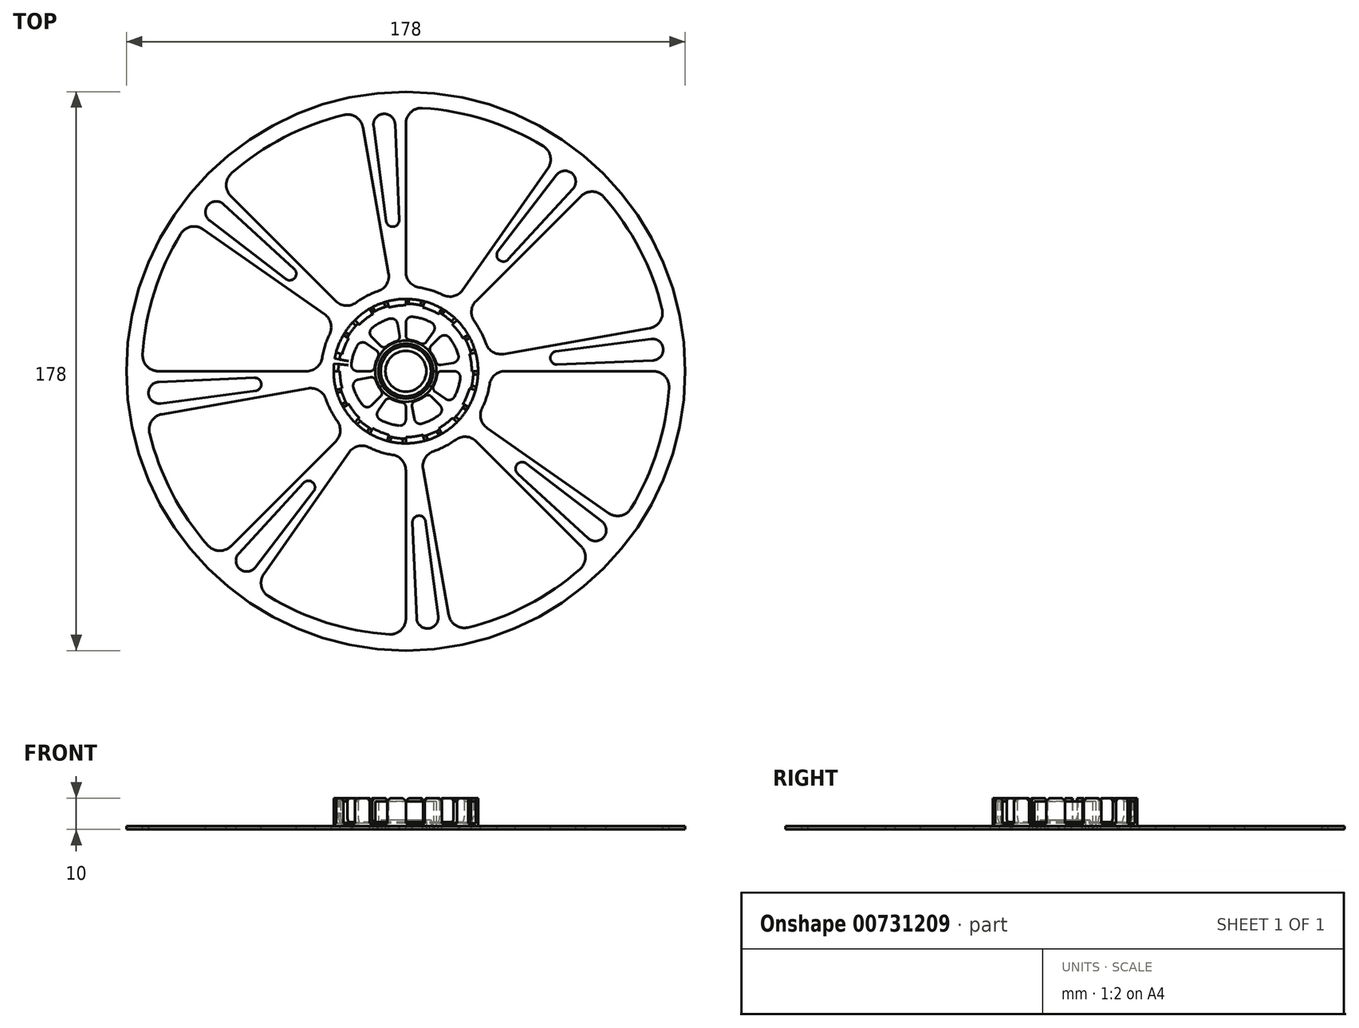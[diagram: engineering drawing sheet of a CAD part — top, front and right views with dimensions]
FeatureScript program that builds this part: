
annotation { "Feature Type Name" : "Feature", "Feature Type Description" : "" }
export const myFeature = defineFeature(function(context is Context, id is Id, definition is map)
    precondition{}
    {
        {
            var Q0;
            Q0=qCreatedBy(makeId("Top.planeOp"),FACE);
            var sketch = newSketch(context, id + "F0", { "sketchPlane" : qUnion([Q0])});
            skCircle(sketch, "E0", {"center": v(0, 0) * mm, "radius": 89 * mm});
            skCircle(sketch, "E1", {"center": v(0, 0) * mm, "radius": 6.5 * mm});
            skSolve(sketch);
        }
        {
            var Q0;
            Q0=qSketchRegion(id+"F0",true);
            extrude(context, id + "F1", {"entities" : qUnion([Q0]), "depth" : 1 * mm, "offsetDistance" : 25 * mm});
        }
        {
            var Q0;
            Q0=makeQuery(id+"F1.opExtrude","CAP_FACE",FACE,{"disambiguationData":[OSD([sQuery(id+"F0.wireOp",EDGE,"E0"),sQuery(id+"F0.wireOp",EDGE,"E1")])],"isStart":false});
            var sketch = newSketch(context, id + "F2", { "sketchPlane" : qUnion([Q0])});
            skCircle(sketch, "E2", {"center": v(0, 0) * mm, "radius": 23 * mm});
            skCircle(sketch, "E3.0", {"center": v(0, 0) * mm, "radius": 21.5 * mm});
            skSolve(sketch);
        }
        {
            var Q0;
            Q0=qSketchRegion(id+"F2",true);
            extrude(context, id + "F3", {"entities" : qUnion([Q0]), "operationType" : NewBodyOperationType.ADD, "depth" : 9 * mm, "offsetDistance" : 25 * mm});
        }
        {
            var Q0;
            Q0=makeQuery(id+"F3.opExtrude","CAP_EDGE",EDGE,{"disambiguationData":[OSD([sQuery(id+"F2.wireOp",EDGE,"E3.0")])],"isStart":true});
            fillet(context, id + "F4", {"entities" : qUnion([Q0]), "radius" : 3 * mm, "tangentPropagation" : true, "allowEdgeOverflow" : false});
        }
        {
            var Q0;
            {var subQ0=sQuery(id+"F0.wireOp",EDGE,"E0");Q0=makeQuery(id+"F3.boolean.opBoolean","SPLIT",FACE,{"disambiguationData":[TD([makeQuery(id+"F1.opExtrude","SWEPT_FACE",FACE,{"disambiguationData":[OSD([subQ0])]})])],"derivedFrom":makeQuery(id+"F1.opExtrude","CAP_FACE",FACE,{"disambiguationData":[OSD([subQ0,sQuery(id+"F0.wireOp",EDGE,"E1")])],"isStart":false})});}
            var sketch = newSketch(context, id + "F5", { "sketchPlane" : qUnion([Q0])});
            skLineSegment(sketch, "E4", {"start": v(-78.84, 0) * mm, "end": v(-31.6, 0) * mm});
            skLineSegment(sketch, "E5", {"start": v(-64.58, 45.22) * mm, "end": v(-25.9, 18.13) * mm});
            skPoint(sketch, "E6.center", {"position": v(0, 0) * mm});
            skArc(sketch, "E7", {"start": v(-26.67, 4.22) * mm, "mid": v(-25.75, 8.12) * mm, "end": v(-24.27, 11.84) * mm});
            skArc(sketch, "E8", {"start": v(-83.83, 5.32) * mm, "mid": v(-80.11, 25.26) * mm, "end": v(-71.72, 43.73) * mm});
            skPoint(sketch, "E9.visualSharp", {"position": v(-68.8, 48.18) * mm});
            skArc(sketch, "E9.filletArc", {"start": v(-64.58, 45.22) * mm, "mid": v(-68.47, 46.02) * mm, "end": v(-71.72, 43.73) * mm});
            skPoint(sketch, "E10.visualSharp", {"position": v(-84, 0) * mm});
            skArc(sketch, "E10.filletArc", {"start": v(-83.83, 5.32) * mm, "mid": v(-82.49, 1.58) * mm, "end": v(-78.84, 0) * mm});
            skPoint(sketch, "E11.visualSharp", {"position": v(-22.12, 15.49) * mm});
            skArc(sketch, "E11.filletArc", {"start": v(-24.27, 11.84) * mm, "mid": v(-23.92, 15.28) * mm, "end": v(-25.9, 18.13) * mm});
            skPoint(sketch, "E12.visualSharp", {"position": v(-27, 0) * mm});
            skArc(sketch, "E12.filletArc", {"start": v(-31.6, 0) * mm, "mid": v(-28.36, 1.2) * mm, "end": v(-26.67, 4.22) * mm});
            skArc(sketch, "E13.1.0", {"start": v(-63.04, -55.52) * mm, "mid": v(-74.5, -38.79) * mm, "end": v(-81.63, -19.8) * mm});
            skArc(sketch, "E13.1.1", {"start": v(-21.84, -15.87) * mm, "mid": v(-23.95, -12.47) * mm, "end": v(-25.53, -8.79) * mm});
            skPoint(sketch, "E13.1.2", {"position": v(-26.59, -4.69) * mm});
            skPoint(sketch, "E13.1.3", {"position": v(-59.4, -59.4) * mm});
            skPoint(sketch, "E13.1.4", {"position": v(-19.1, -19.1) * mm});
            skLineSegment(sketch, "E13.1.5", {"start": v(-31.13, -5.49) * mm, "end": v(-77.64, -13.7) * mm});
            skPoint(sketch, "E13.1.6", {"position": v(-82.72, -14.59) * mm});
            skLineSegment(sketch, "E13.1.7", {"start": v(-55.75, -55.75) * mm, "end": v(-22.35, -22.35) * mm});
            skArc(sketch, "E13.1.8", {"start": v(-63.04, -55.52) * mm, "mid": v(-59.44, -57.21) * mm, "end": v(-55.75, -55.75) * mm});
            skArc(sketch, "E13.1.9", {"start": v(-22.35, -22.35) * mm, "mid": v(-20.9, -19.2) * mm, "end": v(-21.84, -15.87) * mm});
            skArc(sketch, "E13.1.10", {"start": v(-25.53, -8.79) * mm, "mid": v(-27.72, -6.1) * mm, "end": v(-31.13, -5.49) * mm});
            skArc(sketch, "E13.1.11", {"start": v(-77.64, -13.7) * mm, "mid": v(-80.96, -15.88) * mm, "end": v(-81.63, -19.8) * mm});
            skArc(sketch, "E13.2.0", {"start": v(-5.32, -83.83) * mm, "mid": v(-25.26, -80.11) * mm, "end": v(-43.73, -71.72) * mm});
            skArc(sketch, "E13.2.1", {"start": v(-4.22, -26.67) * mm, "mid": v(-8.12, -25.75) * mm, "end": v(-11.84, -24.27) * mm});
            skPoint(sketch, "E13.2.2", {"position": v(-15.49, -22.12) * mm});
            skPoint(sketch, "E13.2.3", {"position": v(0, -84) * mm});
            skPoint(sketch, "E13.2.4", {"position": v(0, -27) * mm});
            skLineSegment(sketch, "E13.2.5", {"start": v(-45.22, -64.58) * mm, "end": v(-18.13, -25.9) * mm});
            skPoint(sketch, "E13.2.6", {"position": v(-48.18, -68.8) * mm});
            skLineSegment(sketch, "E13.2.7", {"start": v(0, -78.84) * mm, "end": v(0, -31.6) * mm});
            skArc(sketch, "E13.2.8", {"start": v(-5.32, -83.83) * mm, "mid": v(-1.58, -82.49) * mm, "end": v(0, -78.84) * mm});
            skArc(sketch, "E13.2.9", {"start": v(0, -31.6) * mm, "mid": v(-1.2, -28.36) * mm, "end": v(-4.22, -26.67) * mm});
            skArc(sketch, "E13.2.10", {"start": v(-11.84, -24.27) * mm, "mid": v(-15.28, -23.92) * mm, "end": v(-18.13, -25.9) * mm});
            skArc(sketch, "E13.2.11", {"start": v(-45.22, -64.58) * mm, "mid": v(-46.02, -68.47) * mm, "end": v(-43.73, -71.72) * mm});
            skArc(sketch, "E13.3.0", {"start": v(55.52, -63.04) * mm, "mid": v(38.79, -74.5) * mm, "end": v(19.8, -81.63) * mm});
            skArc(sketch, "E13.3.1", {"start": v(15.87, -21.84) * mm, "mid": v(12.47, -23.95) * mm, "end": v(8.79, -25.53) * mm});
            skPoint(sketch, "E13.3.2", {"position": v(4.69, -26.59) * mm});
            skPoint(sketch, "E13.3.3", {"position": v(59.4, -59.4) * mm});
            skPoint(sketch, "E13.3.4", {"position": v(19.1, -19.1) * mm});
            skLineSegment(sketch, "E13.3.5", {"start": v(5.49, -31.13) * mm, "end": v(13.7, -77.64) * mm});
            skPoint(sketch, "E13.3.6", {"position": v(14.59, -82.72) * mm});
            skLineSegment(sketch, "E13.3.7", {"start": v(55.75, -55.75) * mm, "end": v(22.35, -22.35) * mm});
            skArc(sketch, "E13.3.8", {"start": v(55.52, -63.04) * mm, "mid": v(57.21, -59.44) * mm, "end": v(55.75, -55.75) * mm});
            skArc(sketch, "E13.3.9", {"start": v(22.35, -22.35) * mm, "mid": v(19.2, -20.9) * mm, "end": v(15.87, -21.84) * mm});
            skArc(sketch, "E13.3.10", {"start": v(8.79, -25.53) * mm, "mid": v(6.1, -27.72) * mm, "end": v(5.49, -31.13) * mm});
            skArc(sketch, "E13.3.11", {"start": v(13.7, -77.64) * mm, "mid": v(15.88, -80.96) * mm, "end": v(19.8, -81.63) * mm});
            skArc(sketch, "E13.4.0", {"start": v(83.83, -5.32) * mm, "mid": v(80.11, -25.26) * mm, "end": v(71.72, -43.73) * mm});
            skArc(sketch, "E13.4.1", {"start": v(26.67, -4.22) * mm, "mid": v(25.75, -8.12) * mm, "end": v(24.27, -11.84) * mm});
            skPoint(sketch, "E13.4.2", {"position": v(22.12, -15.49) * mm});
            skPoint(sketch, "E13.4.3", {"position": v(84, 0) * mm});
            skPoint(sketch, "E13.4.4", {"position": v(27, 0) * mm});
            skLineSegment(sketch, "E13.4.5", {"start": v(64.58, -45.22) * mm, "end": v(25.9, -18.13) * mm});
            skPoint(sketch, "E13.4.6", {"position": v(68.8, -48.18) * mm});
            skLineSegment(sketch, "E13.4.7", {"start": v(78.84, 0) * mm, "end": v(31.6, 0) * mm});
            skArc(sketch, "E13.4.8", {"start": v(83.83, -5.32) * mm, "mid": v(82.49, -1.58) * mm, "end": v(78.84, 0) * mm});
            skArc(sketch, "E13.4.9", {"start": v(31.6, 0) * mm, "mid": v(28.36, -1.2) * mm, "end": v(26.67, -4.22) * mm});
            skArc(sketch, "E13.4.10", {"start": v(24.27, -11.84) * mm, "mid": v(23.92, -15.28) * mm, "end": v(25.9, -18.13) * mm});
            skArc(sketch, "E13.4.11", {"start": v(64.58, -45.22) * mm, "mid": v(68.47, -46.02) * mm, "end": v(71.72, -43.73) * mm});
            skArc(sketch, "E13.5.0", {"start": v(63.04, 55.52) * mm, "mid": v(74.5, 38.79) * mm, "end": v(81.63, 19.8) * mm});
            skArc(sketch, "E13.5.1", {"start": v(21.84, 15.87) * mm, "mid": v(23.95, 12.47) * mm, "end": v(25.53, 8.79) * mm});
            skPoint(sketch, "E13.5.2", {"position": v(26.59, 4.69) * mm});
            skPoint(sketch, "E13.5.3", {"position": v(59.4, 59.4) * mm});
            skPoint(sketch, "E13.5.4", {"position": v(19.1, 19.1) * mm});
            skLineSegment(sketch, "E13.5.5", {"start": v(31.13, 5.49) * mm, "end": v(77.64, 13.7) * mm});
            skPoint(sketch, "E13.5.6", {"position": v(82.72, 14.59) * mm});
            skLineSegment(sketch, "E13.5.7", {"start": v(55.75, 55.75) * mm, "end": v(22.35, 22.35) * mm});
            skArc(sketch, "E13.5.8", {"start": v(63.04, 55.52) * mm, "mid": v(59.44, 57.21) * mm, "end": v(55.75, 55.75) * mm});
            skArc(sketch, "E13.5.9", {"start": v(22.35, 22.35) * mm, "mid": v(20.9, 19.2) * mm, "end": v(21.84, 15.87) * mm});
            skArc(sketch, "E13.5.10", {"start": v(25.53, 8.79) * mm, "mid": v(27.72, 6.1) * mm, "end": v(31.13, 5.49) * mm});
            skArc(sketch, "E13.5.11", {"start": v(77.64, 13.7) * mm, "mid": v(80.96, 15.88) * mm, "end": v(81.63, 19.8) * mm});
            skArc(sketch, "E13.6.0", {"start": v(5.32, 83.83) * mm, "mid": v(25.26, 80.11) * mm, "end": v(43.73, 71.72) * mm});
            skArc(sketch, "E13.6.1", {"start": v(4.22, 26.67) * mm, "mid": v(8.12, 25.75) * mm, "end": v(11.84, 24.27) * mm});
            skPoint(sketch, "E13.6.2", {"position": v(15.49, 22.12) * mm});
            skPoint(sketch, "E13.6.3", {"position": v(0, 84) * mm});
            skPoint(sketch, "E13.6.4", {"position": v(0, 27) * mm});
            skLineSegment(sketch, "E13.6.5", {"start": v(45.22, 64.58) * mm, "end": v(18.13, 25.9) * mm});
            skPoint(sketch, "E13.6.6", {"position": v(48.18, 68.8) * mm});
            skLineSegment(sketch, "E13.6.7", {"start": v(0, 78.84) * mm, "end": v(0, 31.6) * mm});
            skArc(sketch, "E13.6.8", {"start": v(5.32, 83.83) * mm, "mid": v(1.58, 82.49) * mm, "end": v(0, 78.84) * mm});
            skArc(sketch, "E13.6.9", {"start": v(0, 31.6) * mm, "mid": v(1.2, 28.36) * mm, "end": v(4.22, 26.67) * mm});
            skArc(sketch, "E13.6.10", {"start": v(11.84, 24.27) * mm, "mid": v(15.28, 23.92) * mm, "end": v(18.13, 25.9) * mm});
            skArc(sketch, "E13.6.11", {"start": v(45.22, 64.58) * mm, "mid": v(46.02, 68.47) * mm, "end": v(43.73, 71.72) * mm});
            skArc(sketch, "E13.7.0", {"start": v(-55.52, 63.04) * mm, "mid": v(-38.79, 74.5) * mm, "end": v(-19.8, 81.63) * mm});
            skArc(sketch, "E13.7.1", {"start": v(-15.87, 21.84) * mm, "mid": v(-12.47, 23.95) * mm, "end": v(-8.79, 25.53) * mm});
            skPoint(sketch, "E13.7.2", {"position": v(-4.69, 26.59) * mm});
            skPoint(sketch, "E13.7.3", {"position": v(-59.4, 59.4) * mm});
            skPoint(sketch, "E13.7.4", {"position": v(-19.1, 19.1) * mm});
            skLineSegment(sketch, "E13.7.5", {"start": v(-5.49, 31.13) * mm, "end": v(-13.7, 77.64) * mm});
            skPoint(sketch, "E13.7.6", {"position": v(-14.59, 82.72) * mm});
            skLineSegment(sketch, "E13.7.7", {"start": v(-55.75, 55.75) * mm, "end": v(-22.35, 22.35) * mm});
            skArc(sketch, "E13.7.8", {"start": v(-55.52, 63.04) * mm, "mid": v(-57.21, 59.44) * mm, "end": v(-55.75, 55.75) * mm});
            skArc(sketch, "E13.7.9", {"start": v(-22.35, 22.35) * mm, "mid": v(-19.2, 20.9) * mm, "end": v(-15.87, 21.84) * mm});
            skArc(sketch, "E13.7.10", {"start": v(-8.79, 25.53) * mm, "mid": v(-6.1, 27.72) * mm, "end": v(-5.49, 31.13) * mm});
            skArc(sketch, "E13.7.11", {"start": v(-13.7, 77.64) * mm, "mid": v(-15.88, 80.96) * mm, "end": v(-19.8, 81.63) * mm});
            skLineSegment(sketch, "E14", {"start": v(-15.37, 0) * mm, "end": v(-11.4, 0) * mm});
            skLineSegment(sketch, "E15", {"start": v(-12.6, 8.82) * mm, "end": v(-9.34, 6.54) * mm});
            skArc(sketch, "E16", {"start": v(-9.91, 1.3) * mm, "mid": v(-9.54, 3) * mm, "end": v(-8.87, 4.62) * mm});
            skArc(sketch, "E17", {"start": v(-17.35, 2.26) * mm, "mid": v(-16.7, 5.26) * mm, "end": v(-15.51, 8.1) * mm});
            skPoint(sketch, "E18.visualSharp", {"position": v(-14.34, 10.04) * mm});
            skArc(sketch, "E18.filletArc", {"start": v(-12.6, 8.82) * mm, "mid": v(-14.21, 9.12) * mm, "end": v(-15.51, 8.1) * mm});
            skPoint(sketch, "E19.visualSharp", {"position": v(-17.5, 0) * mm});
            skArc(sketch, "E19.filletArc", {"start": v(-17.35, 2.26) * mm, "mid": v(-16.87, 0.68) * mm, "end": v(-15.37, 0) * mm});
            skPoint(sketch, "E20.visualSharp", {"position": v(-10, 0) * mm});
            skArc(sketch, "E20.filletArc", {"start": v(-11.4, 0) * mm, "mid": v(-10.41, 0.37) * mm, "end": v(-9.91, 1.3) * mm});
            skPoint(sketch, "E21.visualSharp", {"position": v(-8.2, 5.74) * mm});
            skArc(sketch, "E21.filletArc", {"start": v(-8.87, 4.62) * mm, "mid": v(-8.74, 5.67) * mm, "end": v(-9.34, 6.54) * mm});
            skPoint(sketch, "E22.1.0", {"position": v(-12.37, -12.37) * mm});
            skPoint(sketch, "E22.1.1", {"position": v(-17.23, -3.04) * mm});
            skArc(sketch, "E22.1.2", {"start": v(-13.87, -10.67) * mm, "mid": v(-15.52, -8.08) * mm, "end": v(-16.7, -5.24) * mm});
            skArc(sketch, "E22.1.3", {"start": v(-7.93, -6.09) * mm, "mid": v(-8.87, -4.62) * mm, "end": v(-9.54, -3) * mm});
            skPoint(sketch, "E22.1.4", {"position": v(-7.07, -7.07) * mm});
            skLineSegment(sketch, "E22.1.5", {"start": v(-11.23, -1.98) * mm, "end": v(-15.14, -2.67) * mm});
            skLineSegment(sketch, "E22.1.6", {"start": v(-10.87, -10.87) * mm, "end": v(-8.06, -8.06) * mm});
            skArc(sketch, "E22.1.7", {"start": v(-13.87, -10.67) * mm, "mid": v(-12.41, -11.45) * mm, "end": v(-10.87, -10.87) * mm});
            skArc(sketch, "E22.1.8", {"start": v(-15.14, -2.67) * mm, "mid": v(-16.5, -3.6) * mm, "end": v(-16.7, -5.24) * mm});
            skPoint(sketch, "E22.1.9", {"position": v(-9.85, -1.74) * mm});
            skArc(sketch, "E22.1.10", {"start": v(-8.06, -8.06) * mm, "mid": v(-7.63, -7.1) * mm, "end": v(-7.93, -6.09) * mm});
            skArc(sketch, "E22.1.11", {"start": v(-9.54, -3) * mm, "mid": v(-10.19, -2.17) * mm, "end": v(-11.23, -1.98) * mm});
            skPoint(sketch, "E22.2.0", {"position": v(0, -17.5) * mm});
            skPoint(sketch, "E22.2.1", {"position": v(-10.04, -14.34) * mm});
            skArc(sketch, "E22.2.2", {"start": v(-2.26, -17.35) * mm, "mid": v(-5.26, -16.7) * mm, "end": v(-8.1, -15.51) * mm});
            skArc(sketch, "E22.2.3", {"start": v(-1.3, -9.91) * mm, "mid": v(-3, -9.54) * mm, "end": v(-4.62, -8.87) * mm});
            skPoint(sketch, "E22.2.4", {"position": v(0, -10) * mm});
            skLineSegment(sketch, "E22.2.5", {"start": v(-8.82, -12.6) * mm, "end": v(-6.54, -9.34) * mm});
            skLineSegment(sketch, "E22.2.6", {"start": v(0, -15.37) * mm, "end": v(0, -11.4) * mm});
            skArc(sketch, "E22.2.7", {"start": v(-2.26, -17.35) * mm, "mid": v(-0.68, -16.87) * mm, "end": v(0, -15.37) * mm});
            skArc(sketch, "E22.2.8", {"start": v(-8.82, -12.6) * mm, "mid": v(-9.12, -14.21) * mm, "end": v(-8.1, -15.51) * mm});
            skPoint(sketch, "E22.2.9", {"position": v(-5.74, -8.2) * mm});
            skArc(sketch, "E22.2.10", {"start": v(0, -11.4) * mm, "mid": v(-0.37, -10.41) * mm, "end": v(-1.3, -9.91) * mm});
            skArc(sketch, "E22.2.11", {"start": v(-4.62, -8.87) * mm, "mid": v(-5.67, -8.74) * mm, "end": v(-6.54, -9.34) * mm});
            skPoint(sketch, "E22.3.0", {"position": v(12.37, -12.37) * mm});
            skPoint(sketch, "E22.3.1", {"position": v(3.04, -17.23) * mm});
            skArc(sketch, "E22.3.2", {"start": v(10.67, -13.87) * mm, "mid": v(8.08, -15.52) * mm, "end": v(5.24, -16.7) * mm});
            skArc(sketch, "E22.3.3", {"start": v(6.09, -7.93) * mm, "mid": v(4.62, -8.87) * mm, "end": v(3, -9.54) * mm});
            skPoint(sketch, "E22.3.4", {"position": v(7.07, -7.07) * mm});
            skLineSegment(sketch, "E22.3.5", {"start": v(1.98, -11.23) * mm, "end": v(2.67, -15.14) * mm});
            skLineSegment(sketch, "E22.3.6", {"start": v(10.87, -10.87) * mm, "end": v(8.06, -8.06) * mm});
            skArc(sketch, "E22.3.7", {"start": v(10.67, -13.87) * mm, "mid": v(11.45, -12.41) * mm, "end": v(10.87, -10.87) * mm});
            skArc(sketch, "E22.3.8", {"start": v(2.67, -15.14) * mm, "mid": v(3.6, -16.5) * mm, "end": v(5.24, -16.7) * mm});
            skPoint(sketch, "E22.3.9", {"position": v(1.74, -9.85) * mm});
            skArc(sketch, "E22.3.10", {"start": v(8.06, -8.06) * mm, "mid": v(7.1, -7.63) * mm, "end": v(6.09, -7.93) * mm});
            skArc(sketch, "E22.3.11", {"start": v(3, -9.54) * mm, "mid": v(2.17, -10.19) * mm, "end": v(1.98, -11.23) * mm});
            skPoint(sketch, "E22.4.0", {"position": v(17.5, 0) * mm});
            skPoint(sketch, "E22.4.1", {"position": v(14.34, -10.04) * mm});
            skArc(sketch, "E22.4.2", {"start": v(17.35, -2.26) * mm, "mid": v(16.7, -5.26) * mm, "end": v(15.51, -8.1) * mm});
            skArc(sketch, "E22.4.3", {"start": v(9.91, -1.3) * mm, "mid": v(9.54, -3) * mm, "end": v(8.87, -4.62) * mm});
            skPoint(sketch, "E22.4.4", {"position": v(10, 0) * mm});
            skLineSegment(sketch, "E22.4.5", {"start": v(12.6, -8.82) * mm, "end": v(9.34, -6.54) * mm});
            skLineSegment(sketch, "E22.4.6", {"start": v(15.37, 0) * mm, "end": v(11.4, 0) * mm});
            skArc(sketch, "E22.4.7", {"start": v(17.35, -2.26) * mm, "mid": v(16.87, -0.68) * mm, "end": v(15.37, 0) * mm});
            skArc(sketch, "E22.4.8", {"start": v(12.6, -8.82) * mm, "mid": v(14.21, -9.12) * mm, "end": v(15.51, -8.1) * mm});
            skPoint(sketch, "E22.4.9", {"position": v(8.2, -5.74) * mm});
            skArc(sketch, "E22.4.10", {"start": v(11.4, 0) * mm, "mid": v(10.41, -0.37) * mm, "end": v(9.91, -1.3) * mm});
            skArc(sketch, "E22.4.11", {"start": v(8.87, -4.62) * mm, "mid": v(8.74, -5.67) * mm, "end": v(9.34, -6.54) * mm});
            skPoint(sketch, "E22.5.0", {"position": v(12.37, 12.37) * mm});
            skPoint(sketch, "E22.5.1", {"position": v(17.23, 3.04) * mm});
            skArc(sketch, "E22.5.2", {"start": v(13.87, 10.67) * mm, "mid": v(15.52, 8.08) * mm, "end": v(16.7, 5.24) * mm});
            skArc(sketch, "E22.5.3", {"start": v(7.93, 6.09) * mm, "mid": v(8.87, 4.62) * mm, "end": v(9.54, 3) * mm});
            skPoint(sketch, "E22.5.4", {"position": v(7.07, 7.07) * mm});
            skLineSegment(sketch, "E22.5.5", {"start": v(11.23, 1.98) * mm, "end": v(15.14, 2.67) * mm});
            skLineSegment(sketch, "E22.5.6", {"start": v(10.87, 10.87) * mm, "end": v(8.06, 8.06) * mm});
            skArc(sketch, "E22.5.7", {"start": v(13.87, 10.67) * mm, "mid": v(12.41, 11.45) * mm, "end": v(10.87, 10.87) * mm});
            skArc(sketch, "E22.5.8", {"start": v(15.14, 2.67) * mm, "mid": v(16.5, 3.6) * mm, "end": v(16.7, 5.24) * mm});
            skPoint(sketch, "E22.5.9", {"position": v(9.85, 1.74) * mm});
            skArc(sketch, "E22.5.10", {"start": v(8.06, 8.06) * mm, "mid": v(7.63, 7.1) * mm, "end": v(7.93, 6.09) * mm});
            skArc(sketch, "E22.5.11", {"start": v(9.54, 3) * mm, "mid": v(10.19, 2.17) * mm, "end": v(11.23, 1.98) * mm});
            skPoint(sketch, "E23.0.6.0", {"position": v(0, 17.5) * mm});
            skPoint(sketch, "E23.1.6.0", {"position": v(10.04, 14.34) * mm});
            skArc(sketch, "E23.2.6.0", {"start": v(2.26, 17.35) * mm, "mid": v(5.26, 16.7) * mm, "end": v(8.1, 15.51) * mm});
            skArc(sketch, "E23.6.6.0", {"start": v(1.3, 9.91) * mm, "mid": v(3, 9.54) * mm, "end": v(4.62, 8.87) * mm});
            skPoint(sketch, "E23.10.6.0", {"position": v(0, 10) * mm});
            skLineSegment(sketch, "E23.11.6.0", {"start": v(8.82, 12.6) * mm, "end": v(6.54, 9.34) * mm});
            skLineSegment(sketch, "E23.14.6.0", {"start": v(0, 15.37) * mm, "end": v(0, 11.4) * mm});
            skArc(sketch, "E23.17.6.0", {"start": v(2.26, 17.35) * mm, "mid": v(0.68, 16.87) * mm, "end": v(0, 15.37) * mm});
            skArc(sketch, "E23.21.6.0", {"start": v(8.82, 12.6) * mm, "mid": v(9.12, 14.21) * mm, "end": v(8.1, 15.51) * mm});
            skPoint(sketch, "E23.25.6.0", {"position": v(5.74, 8.2) * mm});
            skArc(sketch, "E23.26.6.0", {"start": v(0, 11.4) * mm, "mid": v(0.37, 10.41) * mm, "end": v(1.3, 9.91) * mm});
            skArc(sketch, "E23.30.6.0", {"start": v(4.62, 8.87) * mm, "mid": v(5.67, 8.74) * mm, "end": v(6.54, 9.34) * mm});
            skPoint(sketch, "E23.0.7.0", {"position": v(-12.37, 12.37) * mm});
            skPoint(sketch, "E23.1.7.0", {"position": v(-3.04, 17.23) * mm});
            skArc(sketch, "E23.2.7.0", {"start": v(-10.67, 13.87) * mm, "mid": v(-8.08, 15.52) * mm, "end": v(-5.24, 16.7) * mm});
            skArc(sketch, "E23.6.7.0", {"start": v(-6.09, 7.93) * mm, "mid": v(-4.62, 8.87) * mm, "end": v(-3, 9.54) * mm});
            skPoint(sketch, "E23.10.7.0", {"position": v(-7.07, 7.07) * mm});
            skLineSegment(sketch, "E23.11.7.0", {"start": v(-1.98, 11.23) * mm, "end": v(-2.67, 15.14) * mm});
            skLineSegment(sketch, "E23.14.7.0", {"start": v(-10.87, 10.87) * mm, "end": v(-8.06, 8.06) * mm});
            skArc(sketch, "E23.17.7.0", {"start": v(-10.67, 13.87) * mm, "mid": v(-11.45, 12.41) * mm, "end": v(-10.87, 10.87) * mm});
            skArc(sketch, "E23.21.7.0", {"start": v(-2.67, 15.14) * mm, "mid": v(-3.6, 16.5) * mm, "end": v(-5.24, 16.7) * mm});
            skPoint(sketch, "E23.25.7.0", {"position": v(-1.74, 9.85) * mm});
            skArc(sketch, "E23.26.7.0", {"start": v(-8.06, 8.06) * mm, "mid": v(-7.1, 7.63) * mm, "end": v(-6.09, 7.93) * mm});
            skArc(sketch, "E23.30.7.0", {"start": v(-3, 9.54) * mm, "mid": v(-2.17, 10.19) * mm, "end": v(-1.98, 11.23) * mm});
            skLineSegment(sketch, "E24", {"start": v(-62.49, 47.95) * mm, "end": v(-38.3, 29.4) * mm});
            skLineSegment(sketch, "E25", {"start": v(-35.6, 32.62) * mm, "end": v(-58.07, 53.21) * mm});
            skArc(sketch, "E26", {"start": v(-38.3, 29.4) * mm, "mid": v(-35.4, 29.7) * mm, "end": v(-35.6, 32.62) * mm});
            skArc(sketch, "E27", {"start": v(-62.49, 47.95) * mm, "mid": v(-63.03, 52.89) * mm, "end": v(-58.07, 53.21) * mm});
            skArc(sketch, "E28.1.0", {"start": v(-81.1, -19.75) * mm, "mid": v(-80.07, -13.26) * mm, "end": v(-78.54, -6.87) * mm, "construction": true});
            skArc(sketch, "E28.1.1", {"start": v(-47.87, -6.3) * mm, "mid": v(-46.04, -4.03) * mm, "end": v(-48.23, -2.1) * mm});
            skLineSegment(sketch, "E28.1.2", {"start": v(-78.1, -10.28) * mm, "end": v(-47.87, -6.3) * mm});
            skLineSegment(sketch, "E28.1.3", {"start": v(-48.23, -2.1) * mm, "end": v(-78.7, -3.44) * mm});
            skArc(sketch, "E28.1.4", {"start": v(-78.1, -10.28) * mm, "mid": v(-81.97, -7.17) * mm, "end": v(-78.7, -3.44) * mm});
            skArc(sketch, "E28.2.0", {"start": v(-43.38, -71.3) * mm, "mid": v(-47.24, -66) * mm, "end": v(-50.68, -60.4) * mm, "construction": true});
            skArc(sketch, "E28.2.1", {"start": v(-29.4, -38.3) * mm, "mid": v(-29.7, -35.4) * mm, "end": v(-32.62, -35.6) * mm});
            skLineSegment(sketch, "E28.2.2", {"start": v(-47.95, -62.49) * mm, "end": v(-29.4, -38.3) * mm});
            skLineSegment(sketch, "E28.2.3", {"start": v(-32.62, -35.6) * mm, "end": v(-53.21, -58.07) * mm});
            skArc(sketch, "E28.2.4", {"start": v(-47.95, -62.49) * mm, "mid": v(-52.89, -63.03) * mm, "end": v(-53.21, -58.07) * mm});
            skArc(sketch, "E28.3.0", {"start": v(19.75, -81.1) * mm, "mid": v(13.26, -80.07) * mm, "end": v(6.87, -78.54) * mm, "construction": true});
            skArc(sketch, "E28.3.1", {"start": v(6.3, -47.87) * mm, "mid": v(4.03, -46.04) * mm, "end": v(2.1, -48.23) * mm});
            skLineSegment(sketch, "E28.3.2", {"start": v(10.28, -78.1) * mm, "end": v(6.3, -47.87) * mm});
            skLineSegment(sketch, "E28.3.3", {"start": v(2.1, -48.23) * mm, "end": v(3.44, -78.7) * mm});
            skArc(sketch, "E28.3.4", {"start": v(10.28, -78.1) * mm, "mid": v(7.17, -81.97) * mm, "end": v(3.44, -78.7) * mm});
            skArc(sketch, "E28.4.0", {"start": v(71.3, -43.38) * mm, "mid": v(66, -47.24) * mm, "end": v(60.4, -50.68) * mm, "construction": true});
            skArc(sketch, "E28.4.1", {"start": v(38.3, -29.4) * mm, "mid": v(35.4, -29.7) * mm, "end": v(35.6, -32.62) * mm});
            skLineSegment(sketch, "E28.4.2", {"start": v(62.49, -47.95) * mm, "end": v(38.3, -29.4) * mm});
            skLineSegment(sketch, "E28.4.3", {"start": v(35.6, -32.62) * mm, "end": v(58.07, -53.21) * mm});
            skArc(sketch, "E28.4.4", {"start": v(62.49, -47.95) * mm, "mid": v(63.03, -52.89) * mm, "end": v(58.07, -53.21) * mm});
            skArc(sketch, "E28.5.0", {"start": v(81.1, 19.75) * mm, "mid": v(80.07, 13.26) * mm, "end": v(78.54, 6.87) * mm, "construction": true});
            skArc(sketch, "E28.5.1", {"start": v(47.87, 6.3) * mm, "mid": v(46.04, 4.03) * mm, "end": v(48.23, 2.1) * mm});
            skLineSegment(sketch, "E28.5.2", {"start": v(78.1, 10.28) * mm, "end": v(47.87, 6.3) * mm});
            skLineSegment(sketch, "E28.5.3", {"start": v(48.23, 2.1) * mm, "end": v(78.7, 3.44) * mm});
            skArc(sketch, "E28.5.4", {"start": v(78.1, 10.28) * mm, "mid": v(81.97, 7.17) * mm, "end": v(78.7, 3.44) * mm});
            skArc(sketch, "E28.6.0", {"start": v(43.38, 71.3) * mm, "mid": v(47.24, 66) * mm, "end": v(50.68, 60.4) * mm, "construction": true});
            skArc(sketch, "E28.6.1", {"start": v(29.4, 38.3) * mm, "mid": v(29.7, 35.4) * mm, "end": v(32.62, 35.6) * mm});
            skLineSegment(sketch, "E28.6.2", {"start": v(47.95, 62.49) * mm, "end": v(29.4, 38.3) * mm});
            skLineSegment(sketch, "E28.6.3", {"start": v(32.62, 35.6) * mm, "end": v(53.21, 58.07) * mm});
            skArc(sketch, "E28.6.4", {"start": v(47.95, 62.49) * mm, "mid": v(52.89, 63.03) * mm, "end": v(53.21, 58.07) * mm});
            skArc(sketch, "E28.7.0", {"start": v(-19.75, 81.1) * mm, "mid": v(-13.26, 80.07) * mm, "end": v(-6.87, 78.54) * mm, "construction": true});
            skArc(sketch, "E28.7.1", {"start": v(-6.3, 47.87) * mm, "mid": v(-4.03, 46.04) * mm, "end": v(-2.1, 48.23) * mm});
            skLineSegment(sketch, "E28.7.2", {"start": v(-10.28, 78.1) * mm, "end": v(-6.3, 47.87) * mm});
            skLineSegment(sketch, "E28.7.3", {"start": v(-2.1, 48.23) * mm, "end": v(-3.44, 78.7) * mm});
            skArc(sketch, "E28.7.4", {"start": v(-10.28, 78.1) * mm, "mid": v(-7.17, 81.97) * mm, "end": v(-3.44, 78.7) * mm});
            skArc(sketch, "E29", {"start": v(-64.58, 45.22) * mm, "mid": v(-62.55, 48) * mm, "end": v(-60.4, 50.68) * mm, "construction": true});
            skSolve(sketch);
        }
        {
            var Q0;
            Q0=qSketchRegion(id+"F5",true);
            extrude(context, id + "F6", {"entities" : qUnion([Q0]), "operationType" : NewBodyOperationType.REMOVE, "endBound" : BoundingType.UP_TO_NEXT, "oppositeDirection" : true, "depth" : 25 * mm, "offsetDistance" : 25 * mm});
        }
        {
            var Q0;
            {var subQ0=sQuery(id+"F0.wireOp",EDGE,"E1");Q0=makeQuery(id+"F3.boolean.opBoolean","SPLIT",FACE,{"disambiguationData":[TD([makeQuery(id+"F1.opExtrude","SWEPT_FACE",FACE,{"disambiguationData":[OSD([subQ0])]})])],"derivedFrom":makeQuery(id+"F1.opExtrude","CAP_FACE",FACE,{"disambiguationData":[OSD([sQuery(id+"F0.wireOp",EDGE,"E0"),subQ0])],"isStart":false})});}
            var sketch = newSketch(context, id + "F7", { "sketchPlane" : qUnion([Q0])});
            skCircle(sketch, "E30.0", {"center": v(0, 0) * mm, "radius": 8 * mm});
            skCircle(sketch, "E31.0", {"center": v(0, 0) * mm, "radius": 6.5 * mm});
            skSolve(sketch);
        }
        {
            var Q0;
            Q0=qSketchRegion(id+"F7",true);
            extrude(context, id + "F8", {"entities" : qUnion([Q0]), "operationType" : NewBodyOperationType.ADD, "depth" : 2 * mm, "offsetDistance" : 25 * mm});
        }
        {
            var Q0;
            {var subQ0=sQuery(id+"F0.wireOp",EDGE,"E1");Q0=makeQuery(id+"F3.boolean.opBoolean","SPLIT",FACE,{"disambiguationData":[TD([makeQuery(id+"F1.opExtrude","SWEPT_FACE",FACE,{"disambiguationData":[OSD([subQ0])]})])],"derivedFrom":makeQuery(id+"F1.opExtrude","CAP_FACE",FACE,{"disambiguationData":[OSD([sQuery(id+"F0.wireOp",EDGE,"E0"),subQ0])],"isStart":false})});}
            var sketch = newSketch(context, id + "F9", { "sketchPlane" : qUnion([Q0])});
            skCircle(sketch, "E32.0", {"center": v(0, 0) * mm, "radius": 8.75 * mm});
            skCircle(sketch, "E33.0", {"center": v(0, 0) * mm, "radius": 9.75 * mm});
            skSolve(sketch);
        }
        {
            var Q0;
            Q0 = qSketchRegion(id + "F9", true);
            extrude(context, id + "F10", {"entities" : qUnion([Q0]), "operationType" : NewBodyOperationType.ADD, "depth" : 8 * mm, "offsetDistance" : 25 * mm});
        }
        {
            var Q0;
            Q0=makeQuery(id+"F3.opExtrude","CAP_FACE",FACE,{"disambiguationData":[OSD([sQuery(id+"F2.wireOp",EDGE,"E2"),sQuery(id+"F2.wireOp",EDGE,"E3.0")])],"isStart":false});
            var sketch = newSketch(context, id + "F11", { "sketchPlane" : qUnion([Q0])});
            skLineSegment(sketch, "E34", {"start": v(-23.18, 6.21) * mm, "end": v(-20.28, 5.44) * mm});
            skLineSegment(sketch, "E35", {"start": v(-18.19, 10.5) * mm, "end": v(-20.78, 12) * mm});
            skArc(sketch, "E36", {"start": v(-20.28, 5.44) * mm, "mid": v(-19.4, 8.04) * mm, "end": v(-18.19, 10.5) * mm});
            skArc(sketch, "E37", {"start": v(-23.18, 6.21) * mm, "mid": v(-22.17, 9.18) * mm, "end": v(-20.78, 12) * mm});
            skArc(sketch, "E38.1.0", {"start": v(-23.18, -6.21) * mm, "mid": v(-23.8, -3.13) * mm, "end": v(-24, 0) * mm});
            skArc(sketch, "E38.1.1", {"start": v(-20.28, -5.44) * mm, "mid": v(-20.82, -2.74) * mm, "end": v(-21, 0) * mm});
            skLineSegment(sketch, "E38.1.2", {"start": v(-21, 0) * mm, "end": v(-24, 0) * mm});
            skLineSegment(sketch, "E38.1.3", {"start": v(-23.18, -6.21) * mm, "end": v(-20.28, -5.44) * mm});
            skArc(sketch, "E38.2.0", {"start": v(-16.97, -16.97) * mm, "mid": v(-19.04, -14.61) * mm, "end": v(-20.78, -12) * mm});
            skArc(sketch, "E38.2.1", {"start": v(-14.85, -14.85) * mm, "mid": v(-16.66, -12.78) * mm, "end": v(-18.19, -10.5) * mm});
            skLineSegment(sketch, "E38.2.2", {"start": v(-18.19, -10.5) * mm, "end": v(-20.78, -12) * mm});
            skLineSegment(sketch, "E38.2.3", {"start": v(-16.97, -16.97) * mm, "end": v(-14.85, -14.85) * mm});
            skArc(sketch, "E38.3.0", {"start": v(-6.21, -23.18) * mm, "mid": v(-9.18, -22.17) * mm, "end": v(-12, -20.78) * mm});
            skArc(sketch, "E38.3.1", {"start": v(-5.44, -20.28) * mm, "mid": v(-8.04, -19.4) * mm, "end": v(-10.5, -18.19) * mm});
            skLineSegment(sketch, "E38.3.2", {"start": v(-10.5, -18.19) * mm, "end": v(-12, -20.78) * mm});
            skLineSegment(sketch, "E38.3.3", {"start": v(-6.21, -23.18) * mm, "end": v(-5.44, -20.28) * mm});
            skArc(sketch, "E38.4.0", {"start": v(6.21, -23.18) * mm, "mid": v(3.13, -23.8) * mm, "end": v(0, -24) * mm});
            skArc(sketch, "E38.4.1", {"start": v(5.44, -20.28) * mm, "mid": v(2.74, -20.82) * mm, "end": v(0, -21) * mm});
            skLineSegment(sketch, "E38.4.2", {"start": v(0, -21) * mm, "end": v(0, -24) * mm});
            skLineSegment(sketch, "E38.4.3", {"start": v(6.21, -23.18) * mm, "end": v(5.44, -20.28) * mm});
            skArc(sketch, "E38.5.0", {"start": v(16.97, -16.97) * mm, "mid": v(14.61, -19.04) * mm, "end": v(12, -20.78) * mm});
            skArc(sketch, "E38.5.1", {"start": v(14.85, -14.85) * mm, "mid": v(12.78, -16.66) * mm, "end": v(10.5, -18.19) * mm});
            skLineSegment(sketch, "E38.5.2", {"start": v(10.5, -18.19) * mm, "end": v(12, -20.78) * mm});
            skLineSegment(sketch, "E38.5.3", {"start": v(16.97, -16.97) * mm, "end": v(14.85, -14.85) * mm});
            skArc(sketch, "E38.6.0", {"start": v(23.18, -6.21) * mm, "mid": v(22.17, -9.18) * mm, "end": v(20.78, -12) * mm});
            skArc(sketch, "E38.6.1", {"start": v(20.28, -5.44) * mm, "mid": v(19.4, -8.04) * mm, "end": v(18.19, -10.5) * mm});
            skLineSegment(sketch, "E38.6.2", {"start": v(18.19, -10.5) * mm, "end": v(20.78, -12) * mm});
            skLineSegment(sketch, "E38.6.3", {"start": v(23.18, -6.21) * mm, "end": v(20.28, -5.44) * mm});
            skArc(sketch, "E38.7.0", {"start": v(23.18, 6.21) * mm, "mid": v(23.8, 3.13) * mm, "end": v(24, 0) * mm});
            skArc(sketch, "E38.7.1", {"start": v(20.28, 5.44) * mm, "mid": v(20.82, 2.74) * mm, "end": v(21, 0) * mm});
            skLineSegment(sketch, "E38.7.2", {"start": v(21, 0) * mm, "end": v(24, 0) * mm});
            skLineSegment(sketch, "E38.7.3", {"start": v(23.18, 6.21) * mm, "end": v(20.28, 5.44) * mm});
            skArc(sketch, "E38.8.0", {"start": v(16.97, 16.97) * mm, "mid": v(19.04, 14.61) * mm, "end": v(20.78, 12) * mm});
            skArc(sketch, "E38.8.1", {"start": v(14.85, 14.85) * mm, "mid": v(16.66, 12.78) * mm, "end": v(18.19, 10.5) * mm});
            skLineSegment(sketch, "E38.8.2", {"start": v(18.19, 10.5) * mm, "end": v(20.78, 12) * mm});
            skLineSegment(sketch, "E38.8.3", {"start": v(16.97, 16.97) * mm, "end": v(14.85, 14.85) * mm});
            skArc(sketch, "E38.9.0", {"start": v(6.21, 23.18) * mm, "mid": v(9.18, 22.17) * mm, "end": v(12, 20.78) * mm});
            skArc(sketch, "E38.9.1", {"start": v(5.44, 20.28) * mm, "mid": v(8.04, 19.4) * mm, "end": v(10.5, 18.19) * mm});
            skLineSegment(sketch, "E38.9.2", {"start": v(10.5, 18.19) * mm, "end": v(12, 20.78) * mm});
            skLineSegment(sketch, "E38.9.3", {"start": v(6.21, 23.18) * mm, "end": v(5.44, 20.28) * mm});
            skArc(sketch, "E38.10.0", {"start": v(-6.21, 23.18) * mm, "mid": v(-3.13, 23.8) * mm, "end": v(0, 24) * mm});
            skArc(sketch, "E38.10.1", {"start": v(-5.44, 20.28) * mm, "mid": v(-2.74, 20.82) * mm, "end": v(0, 21) * mm});
            skLineSegment(sketch, "E38.10.2", {"start": v(0, 21) * mm, "end": v(0, 24) * mm});
            skLineSegment(sketch, "E38.10.3", {"start": v(-6.21, 23.18) * mm, "end": v(-5.44, 20.28) * mm});
            skArc(sketch, "E38.11.0", {"start": v(-16.97, 16.97) * mm, "mid": v(-14.61, 19.04) * mm, "end": v(-12, 20.78) * mm});
            skArc(sketch, "E38.11.1", {"start": v(-14.85, 14.85) * mm, "mid": v(-12.78, 16.66) * mm, "end": v(-10.5, 18.19) * mm});
            skLineSegment(sketch, "E38.11.2", {"start": v(-10.5, 18.19) * mm, "end": v(-12, 20.78) * mm});
            skLineSegment(sketch, "E38.11.3", {"start": v(-16.97, 16.97) * mm, "end": v(-14.85, 14.85) * mm});
            skSolve(sketch);
        }
        {
            var Q0;
            Q0 = qSketchRegion(id + "F11", true);
            extrude(context, id + "F12", {"entities" : qUnion([Q0]), "operationType" : NewBodyOperationType.REMOVE, "oppositeDirection" : true, "depth" : 8 * mm, "offsetDistance" : 25 * mm});
        }
        {
            var Q0;
            Q0=makeQuery(id+"F10.opExtrude","CAP_EDGE",EDGE,{"disambiguationData":[OSD([sQuery(id+"F9.wireOp",EDGE,"E32.0")])],"isStart":true});
            fillet(context, id + "F13", {"entities" : qUnion([Q0]), "radius" : 1 * mm, "tangentPropagation" : true, "allowEdgeOverflow" : false});
        }
        {
            var Q0;
            {var subQ0=sQuery(id+"F2.wireOp",EDGE,"E2");var subQ1=sQuery(id+"F2.wireOp",EDGE,"E3.0");Q0=makeQuery(id+"F12.boolean.opBoolean","SPLIT",FACE,{"disambiguationData":[TD([makeQuery(id+"F12.opExtrude","SWEPT_FACE",FACE,{"disambiguationData":[OSD([sQuery(id+"F11.wireOp",EDGE,"E34")])]})])],"derivedFrom":makeQuery(id+"F3.opExtrude","CAP_FACE",FACE,{"disambiguationData":[OSD([subQ0,subQ1])],"isStart":false})});}
            var sketch = newSketch(context, id + "F14", { "sketchPlane" : qUnion([Q0])});
            skLineSegment(sketch, "E39", {"start": v(-23.87, 2.5) * mm, "end": v(-13.92, 1.46) * mm});
            skLineSegment(sketch, "E40", {"start": v(-13.92, 1.46) * mm, "end": v(-13.82, 2.44) * mm});
            skLineSegment(sketch, "E41", {"start": v(-13.82, 2.44) * mm, "end": v(-23.67, 4.17) * mm});
            skLineSegment(sketch, "E42", {"start": v(-23.67, 4.17) * mm, "end": v(-23.87, 2.5) * mm});
            skSolve(sketch);
        }
        {
            var Q0;
            Q0 = qSketchRegion(id + "F14", true);
            var Q1;
            {var subQ0=sQuery(id+"F0.wireOp",EDGE,"E0");Q1=makeQuery(id+"F3.boolean.opBoolean","SPLIT",FACE,{"disambiguationData":[TD([makeQuery(id+"F1.opExtrude","SWEPT_FACE",FACE,{"disambiguationData":[OSD([subQ0])]})])],"derivedFrom":makeQuery(id+"F1.opExtrude","CAP_FACE",FACE,{"disambiguationData":[OSD([subQ0,sQuery(id+"F0.wireOp",EDGE,"E1")])],"isStart":false})});}
            extrude(context, id + "F15", {"entities" : qUnion([Q0]), "operationType" : NewBodyOperationType.REMOVE, "endBound" : BoundingType.UP_TO_SURFACE, "oppositeDirection" : true, "depth" : 25 * mm, "endBoundEntityFace" : qUnion([Q1]), "offsetDistance" : 25 * mm});
        }
        {
            var Q0;
            Q0=makeQuery(id+"F12.boolean.opBoolean","COPY",EDGE,{"derivedFrom":makeQuery(id+"F12.opExtrude","CAP_EDGE",EDGE,{"disambiguationData":[OSD([sQuery(id+"F11.wireOp",EDGE,"E38.11.2")])],"isStart":true})});
            var Q1;
            Q1=makeQuery(id+"F12.boolean.opBoolean","COPY",EDGE,{"derivedFrom":makeQuery(id+"F12.opExtrude","CAP_EDGE",EDGE,{"disambiguationData":[OSD([sQuery(id+"F11.wireOp",EDGE,"E38.10.3")])],"isStart":true})});
            var Q2;
            Q2=makeQuery(id+"F12.boolean.opBoolean","COPY",EDGE,{"derivedFrom":makeQuery(id+"F12.opExtrude","CAP_EDGE",EDGE,{"disambiguationData":[OSD([sQuery(id+"F11.wireOp",EDGE,"E38.10.2")])],"isStart":true})});
            var Q3;
            Q3=makeQuery(id+"F12.boolean.opBoolean","COPY",EDGE,{"derivedFrom":makeQuery(id+"F12.opExtrude","CAP_EDGE",EDGE,{"disambiguationData":[OSD([sQuery(id+"F11.wireOp",EDGE,"E38.9.3")])],"isStart":true})});
            var Q4;
            Q4=makeQuery(id+"F12.boolean.opBoolean","COPY",EDGE,{"derivedFrom":makeQuery(id+"F12.opExtrude","CAP_EDGE",EDGE,{"disambiguationData":[OSD([sQuery(id+"F11.wireOp",EDGE,"E38.9.2")])],"isStart":true})});
            var Q5;
            Q5=makeQuery(id+"F12.boolean.opBoolean","COPY",EDGE,{"derivedFrom":makeQuery(id+"F12.opExtrude","CAP_EDGE",EDGE,{"disambiguationData":[OSD([sQuery(id+"F11.wireOp",EDGE,"E38.8.3")])],"isStart":true})});
            var Q6;
            Q6=makeQuery(id+"F12.boolean.opBoolean","COPY",EDGE,{"derivedFrom":makeQuery(id+"F12.opExtrude","CAP_EDGE",EDGE,{"disambiguationData":[OSD([sQuery(id+"F11.wireOp",EDGE,"E38.11.3")])],"isStart":true})});
            var Q7;
            Q7=makeQuery(id+"F12.boolean.opBoolean","COPY",EDGE,{"derivedFrom":makeQuery(id+"F12.opExtrude","CAP_EDGE",EDGE,{"disambiguationData":[OSD([sQuery(id+"F11.wireOp",EDGE,"E35")])],"isStart":true})});
            var Q8;
            Q8=makeQuery(id+"F12.boolean.opBoolean","COPY",EDGE,{"derivedFrom":makeQuery(id+"F12.opExtrude","CAP_EDGE",EDGE,{"disambiguationData":[OSD([sQuery(id+"F11.wireOp",EDGE,"E34")])],"isStart":true})});
            var Q9;
            Q9=makeQuery(id+"F12.boolean.opBoolean","COPY",EDGE,{"derivedFrom":makeQuery(id+"F12.opExtrude","CAP_EDGE",EDGE,{"disambiguationData":[OSD([sQuery(id+"F11.wireOp",EDGE,"E38.1.2")])],"isStart":true})});
            var Q10;
            Q10=makeQuery(id+"F12.boolean.opBoolean","COPY",EDGE,{"derivedFrom":makeQuery(id+"F12.opExtrude","CAP_EDGE",EDGE,{"disambiguationData":[OSD([sQuery(id+"F11.wireOp",EDGE,"E38.1.3")])],"isStart":true})});
            var Q11;
            Q11=makeQuery(id+"F12.boolean.opBoolean","COPY",EDGE,{"derivedFrom":makeQuery(id+"F12.opExtrude","CAP_EDGE",EDGE,{"disambiguationData":[OSD([sQuery(id+"F11.wireOp",EDGE,"E38.2.2")])],"isStart":true})});
            var Q12;
            Q12=makeQuery(id+"F12.boolean.opBoolean","COPY",EDGE,{"derivedFrom":makeQuery(id+"F12.opExtrude","CAP_EDGE",EDGE,{"disambiguationData":[OSD([sQuery(id+"F11.wireOp",EDGE,"E38.2.3")])],"isStart":true})});
            var Q13;
            Q13=makeQuery(id+"F12.boolean.opBoolean","COPY",EDGE,{"derivedFrom":makeQuery(id+"F12.opExtrude","CAP_EDGE",EDGE,{"disambiguationData":[OSD([sQuery(id+"F11.wireOp",EDGE,"E38.3.2")])],"isStart":true})});
            var Q14;
            Q14=makeQuery(id+"F12.boolean.opBoolean","COPY",EDGE,{"derivedFrom":makeQuery(id+"F12.opExtrude","CAP_EDGE",EDGE,{"disambiguationData":[OSD([sQuery(id+"F11.wireOp",EDGE,"E38.3.3")])],"isStart":true})});
            var Q15;
            Q15=makeQuery(id+"F12.boolean.opBoolean","COPY",EDGE,{"derivedFrom":makeQuery(id+"F12.opExtrude","CAP_EDGE",EDGE,{"disambiguationData":[OSD([sQuery(id+"F11.wireOp",EDGE,"E38.4.2")])],"isStart":true})});
            var Q16;
            Q16=makeQuery(id+"F12.boolean.opBoolean","COPY",EDGE,{"derivedFrom":makeQuery(id+"F12.opExtrude","CAP_EDGE",EDGE,{"disambiguationData":[OSD([sQuery(id+"F11.wireOp",EDGE,"E38.4.3")])],"isStart":true})});
            var Q17;
            Q17=makeQuery(id+"F12.boolean.opBoolean","COPY",EDGE,{"derivedFrom":makeQuery(id+"F12.opExtrude","CAP_EDGE",EDGE,{"disambiguationData":[OSD([sQuery(id+"F11.wireOp",EDGE,"E38.5.2")])],"isStart":true})});
            var Q18;
            Q18=makeQuery(id+"F12.boolean.opBoolean","COPY",EDGE,{"derivedFrom":makeQuery(id+"F12.opExtrude","CAP_EDGE",EDGE,{"disambiguationData":[OSD([sQuery(id+"F11.wireOp",EDGE,"E38.5.3")])],"isStart":true})});
            var Q19;
            Q19=makeQuery(id+"F12.boolean.opBoolean","COPY",EDGE,{"derivedFrom":makeQuery(id+"F12.opExtrude","CAP_EDGE",EDGE,{"disambiguationData":[OSD([sQuery(id+"F11.wireOp",EDGE,"E38.6.2")])],"isStart":true})});
            var Q20;
            Q20=makeQuery(id+"F12.boolean.opBoolean","COPY",EDGE,{"derivedFrom":makeQuery(id+"F12.opExtrude","CAP_EDGE",EDGE,{"disambiguationData":[OSD([sQuery(id+"F11.wireOp",EDGE,"E38.6.3")])],"isStart":true})});
            var Q21;
            Q21=makeQuery(id+"F12.boolean.opBoolean","COPY",EDGE,{"derivedFrom":makeQuery(id+"F12.opExtrude","CAP_EDGE",EDGE,{"disambiguationData":[OSD([sQuery(id+"F11.wireOp",EDGE,"E38.7.2")])],"isStart":true})});
            var Q22;
            Q22=makeQuery(id+"F12.boolean.opBoolean","COPY",EDGE,{"derivedFrom":makeQuery(id+"F12.opExtrude","CAP_EDGE",EDGE,{"disambiguationData":[OSD([sQuery(id+"F11.wireOp",EDGE,"E38.7.3")])],"isStart":true})});
            var Q23;
            Q23=makeQuery(id+"F12.boolean.opBoolean","COPY",EDGE,{"derivedFrom":makeQuery(id+"F12.opExtrude","CAP_EDGE",EDGE,{"disambiguationData":[OSD([sQuery(id+"F11.wireOp",EDGE,"E38.8.2")])],"isStart":true})});
            chamfer(context, id + "F16", {"entities" : qUnion([Q0, Q1, Q2, Q3, Q4, Q5, Q6, Q7, Q8, Q9, Q10, Q11, Q12, Q13, Q14, Q15, Q16, Q17, Q18, Q19, Q20, Q21, Q22, Q23]), "width" : 1 * mm, "tangentPropagation" : true});
        }
    });
